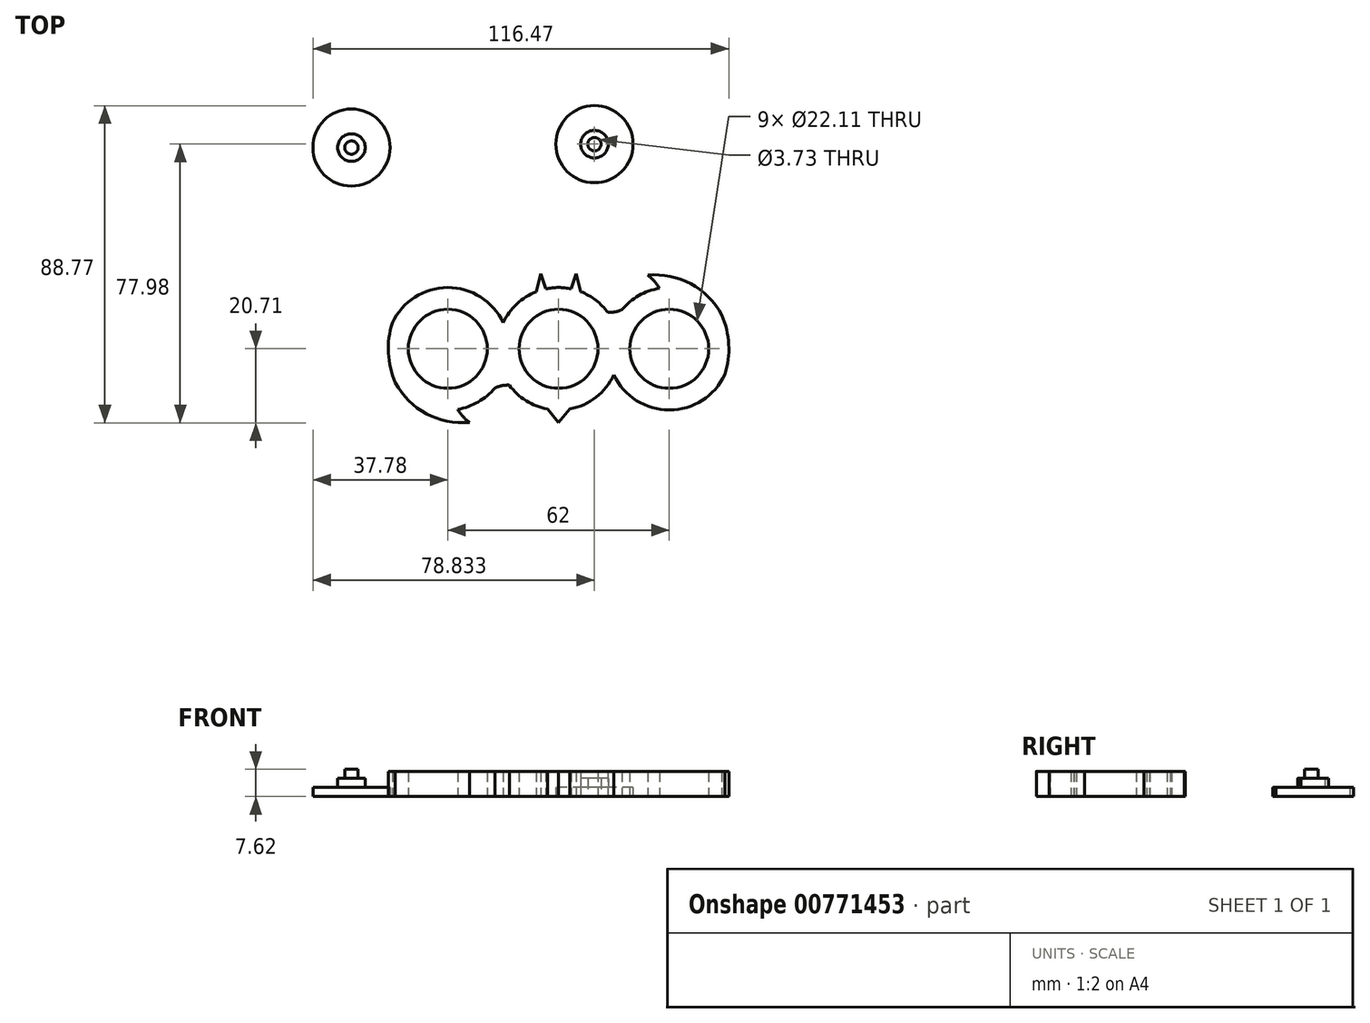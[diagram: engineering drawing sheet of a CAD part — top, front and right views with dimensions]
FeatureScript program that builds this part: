
annotation { "Feature Type Name" : "Feature", "Feature Type Description" : "" }
export const myFeature = defineFeature(function(context is Context, id is Id, definition is map)
    precondition{}
    {
        {
            var Q0;
            Q0=qCreatedBy(makeId("Top.planeOp"),FACE);
            var sketch = newSketch(context, id + "F0", { "sketchPlane" : qUnion([Q0])});
            skCircle(sketch, "E0", {"center": v(31, 0) * mm, "radius": 11.05 * mm});
            skCircle(sketch, "E1", {"center": v(-31, 0) * mm, "radius": 11.05 * mm});
            skCircle(sketch, "E2", {"center": v(0, 0) * mm, "radius": 11.05 * mm});
            skCircle(sketch, "E3", {"center": v(-31, 0) * mm, "radius": 17.15 * mm});
            skCircle(sketch, "E4", {"center": v(31, 0) * mm, "radius": 17.15 * mm});
            skCircle(sketch, "E5", {"center": v(0, 0) * mm, "radius": 17.15 * mm});
            skArc(sketch, "E6", {"start": v(-28.25, 16.92) * mm, "mid": v(-26.8, 18.94) * mm, "end": v(-24.96, 20.62) * mm});
            skArc(sketch, "E7", {"start": v(-24.96, 20.62) * mm, "mid": v(-37.01, 18.18) * mm, "end": v(-45.7, 9.47) * mm});
            skArc(sketch, "E8.MirrorCS", {"start": v(-24.96, -20.62) * mm, "mid": v(-37.01, -18.18) * mm, "end": v(-45.7, -9.47) * mm});
            skArc(sketch, "E9.MirrorCS", {"start": v(-28.25, -16.92) * mm, "mid": v(-26.8, -18.94) * mm, "end": v(-24.96, -20.62) * mm});
            skArc(sketch, "E10.MirrorCS", {"start": v(28.25, 16.92) * mm, "mid": v(26.8, 18.94) * mm, "end": v(24.96, 20.62) * mm});
            skArc(sketch, "E11.MirrorCS", {"start": v(24.96, 20.62) * mm, "mid": v(37.01, 18.18) * mm, "end": v(45.7, 9.47) * mm});
            skArc(sketch, "E12.MirrorCS", {"start": v(24.96, -20.62) * mm, "mid": v(37.01, -18.18) * mm, "end": v(45.7, -9.47) * mm});
            skArc(sketch, "E13.MirrorCS", {"start": v(28.25, -16.92) * mm, "mid": v(26.8, -18.94) * mm, "end": v(24.96, -20.62) * mm});
            skLineSegment(sketch, "E14", {"start": v(-3.1, -16.86) * mm, "end": v(0, -20.62) * mm});
            skLineSegment(sketch, "E15", {"start": v(0, -20.62) * mm, "end": v(3.15, -16.85) * mm});
            skLineSegment(sketch, "E16", {"start": v(-6.23, 15.97) * mm, "end": v(-4.98, 20.95) * mm});
            skLineSegment(sketch, "E17", {"start": v(-4.98, 20.95) * mm, "end": v(-3.55, 16.77) * mm});
            skLineSegment(sketch, "E18.MirrorCS", {"start": v(4.98, 20.95) * mm, "end": v(3.55, 16.77) * mm});
            skLineSegment(sketch, "E19.MirrorCS", {"start": v(6.23, 15.97) * mm, "end": v(4.98, 20.95) * mm});
            skArc(sketch, "E20", {"start": v(-13.8, -10.17) * mm, "mid": v(-15.85, -10.33) * mm, "end": v(-17.8, -10.94) * mm});
            skArc(sketch, "E21.MirrorCS", {"start": v(13.8, -10.17) * mm, "mid": v(15.85, -10.33) * mm, "end": v(17.8, -10.94) * mm});
            skArc(sketch, "E22.MirrorCS", {"start": v(-13.8, 10.17) * mm, "mid": v(-15.85, 10.33) * mm, "end": v(-17.8, 10.94) * mm});
            skArc(sketch, "E23.MirrorCS", {"start": v(13.8, 10.17) * mm, "mid": v(15.85, 10.33) * mm, "end": v(17.8, 10.94) * mm});
            skArc(sketch, "E24", {"start": v(-45.7, 9.47) * mm, "mid": v(-47.69, 0) * mm, "end": v(-45.7, -9.47) * mm});
            skArc(sketch, "E25.MirrorCS", {"start": v(45.7, 9.47) * mm, "mid": v(47.69, 0) * mm, "end": v(45.7, -9.47) * mm});
            skSolve(sketch);
        }
        {
            var Q0;
            {var subQ0=sQuery(id+"F0.wireOp",EDGE,"E6");Q0=makeQuery(id+"F0.imprint","IMPRINT",FACE,{"disambiguationData":[TD([[makeQuery(id+"F0.imprint","IMPRINT",EDGE,{"derivedFrom":subQ0}),1.0]])]});}
            var Q1;
            {var subQ0=sQuery(id+"F0.wireOp",EDGE,"E9.MirrorCS");Q1=makeQuery(id+"F0.imprint","IMPRINT",FACE,{"disambiguationData":[TD([[makeQuery(id+"F0.imprint","IMPRINT",EDGE,{"derivedFrom":subQ0}),-1.0]])]});}
            var Q2;
            {var subQ0=sQuery(id+"F0.wireOp",EDGE,"E22.MirrorCS");Q2=makeQuery(id+"F0.imprint","IMPRINT",FACE,{"disambiguationData":[TD([[makeQuery(id+"F0.imprint","IMPRINT",EDGE,{"derivedFrom":subQ0}),1.0]])]});}
            var Q3;
            {var subQ0=sQuery(id+"F0.wireOp",EDGE,"E5");var subQ1=sQuery(id+"F0.wireOp",EDGE,"E3");var subQ2=makeQuery(id+"F0.imprint","INTERSECT",VERTEX,{"disambiguationData":[OD(0.0)],"derivedFrom":[subQ1,subQ0]});Q3=makeQuery(id+"F0.imprint","IMPRINT",FACE,{"disambiguationData":[TD([[makeQuery(id+"F0.imprint","IMPRINT",EDGE,{"disambiguationData":[TD([[subQ2,1.0]])],"derivedFrom":subQ1}),1.0]])]});}
            var Q4;
            {var subQ0=sQuery(id+"F0.wireOp",EDGE,"E20");Q4=makeQuery(id+"F0.imprint","IMPRINT",FACE,{"disambiguationData":[TD([[makeQuery(id+"F0.imprint","IMPRINT",EDGE,{"derivedFrom":subQ0}),-1.0]])]});}
            var Q5;
            Q5=makeQuery(id+"F0.imprint","IMPRINT",FACE,{"disambiguationData":[TD([[makeQuery(id+"F0.imprint","IMPRINT",EDGE,{"derivedFrom":sQuery(id+"F0.wireOp",EDGE,"E2")}),-1.0]])]});
            var Q6;
            {var subQ0=sQuery(id+"F0.wireOp",EDGE,"E16");Q6=makeQuery(id+"F0.imprint","IMPRINT",FACE,{"disambiguationData":[TD([[makeQuery(id+"F0.imprint","IMPRINT",EDGE,{"derivedFrom":subQ0}),-1.0]])]});}
            var Q7;
            {var subQ0=sQuery(id+"F0.wireOp",EDGE,"E18.MirrorCS");Q7=makeQuery(id+"F0.imprint","IMPRINT",FACE,{"disambiguationData":[TD([[makeQuery(id+"F0.imprint","IMPRINT",EDGE,{"derivedFrom":subQ0}),1.0]])]});}
            var Q8;
            {var subQ0=sQuery(id+"F0.wireOp",EDGE,"E14");Q8=makeQuery(id+"F0.imprint","IMPRINT",FACE,{"disambiguationData":[TD([[makeQuery(id+"F0.imprint","IMPRINT",EDGE,{"derivedFrom":subQ0}),1.0]])]});}
            var Q9;
            {var subQ0=sQuery(id+"F0.wireOp",EDGE,"E5");var subQ1=sQuery(id+"F0.wireOp",EDGE,"E4");var subQ2=makeQuery(id+"F0.imprint","INTERSECT",VERTEX,{"disambiguationData":[OD(0.0)],"derivedFrom":[subQ1,subQ0]});Q9=makeQuery(id+"F0.imprint","IMPRINT",FACE,{"disambiguationData":[TD([[makeQuery(id+"F0.imprint","IMPRINT",EDGE,{"disambiguationData":[TD([[subQ2,-1.0]])],"derivedFrom":subQ1}),1.0]])]});}
            var Q10;
            {var subQ0=sQuery(id+"F0.wireOp",EDGE,"E23.MirrorCS");Q10=makeQuery(id+"F0.imprint","IMPRINT",FACE,{"disambiguationData":[TD([[makeQuery(id+"F0.imprint","IMPRINT",EDGE,{"derivedFrom":subQ0}),-1.0]])]});}
            var Q11;
            {var subQ0=sQuery(id+"F0.wireOp",EDGE,"E21.MirrorCS");Q11=makeQuery(id+"F0.imprint","IMPRINT",FACE,{"disambiguationData":[TD([[makeQuery(id+"F0.imprint","IMPRINT",EDGE,{"derivedFrom":subQ0}),1.0]])]});}
            var Q12;
            Q12=makeQuery(id+"F0.imprint","IMPRINT",FACE,{"disambiguationData":[TD([[makeQuery(id+"F0.imprint","IMPRINT",EDGE,{"derivedFrom":sQuery(id+"F0.wireOp",EDGE,"E0")}),-1.0]])]});
            var Q13;
            {var subQ0=sQuery(id+"F0.wireOp",EDGE,"E10.MirrorCS");Q13=makeQuery(id+"F0.imprint","IMPRINT",FACE,{"disambiguationData":[TD([[makeQuery(id+"F0.imprint","IMPRINT",EDGE,{"derivedFrom":subQ0}),-1.0]])]});}
            var Q14;
            {var subQ0=sQuery(id+"F0.wireOp",EDGE,"E13.MirrorCS");Q14=makeQuery(id+"F0.imprint","IMPRINT",FACE,{"disambiguationData":[TD([[makeQuery(id+"F0.imprint","IMPRINT",EDGE,{"derivedFrom":subQ0}),1.0]])]});}
            var Q15;
            Q15=makeQuery(id+"F0.imprint","IMPRINT",FACE,{"disambiguationData":[TD([[makeQuery(id+"F0.imprint","IMPRINT",EDGE,{"derivedFrom":sQuery(id+"F0.wireOp",EDGE,"E1")}),-1.0]])]});
            extrude(context, id + "F1", {"entities" : qUnion([Q0, Q1, Q2, Q3, Q4, Q5, Q6, Q7, Q8, Q9, Q10, Q11, Q12, Q13, Q14, Q15]), "depth" : 7.04 * mm, "offsetDistance" : 25.4 * mm});
        }
        {
            var Q0;
            Q0=qCreatedBy(makeId("Top.planeOp"),FACE);
            var sketch = newSketch(context, id + "F2", { "sketchPlane" : qUnion([Q0])});
            skCircle(sketch, "E26", {"center": v(-57.99, 56.32) * mm, "radius": 10.8 * mm});
            skCircle(sketch, "E27", {"center": v(-57.99, 56.32) * mm, "radius": 3.86 * mm});
            skCircle(sketch, "E28", {"center": v(-57.99, 56.32) * mm, "radius": 1.87 * mm});
            skCircle(sketch, "E29", {"center": v(10.05, 57.27) * mm, "radius": 10.8 * mm});
            skCircle(sketch, "E30", {"center": v(10.05, 57.27) * mm, "radius": 3.86 * mm});
            skCircle(sketch, "E31", {"center": v(10.05, 57.27) * mm, "radius": 1.87 * mm});
            skSolve(sketch);
        }
        {
            var Q0;
            Q0=makeQuery(id+"F2.imprint","IMPRINT",FACE,{"disambiguationData":[TD([[makeQuery(id+"F2.imprint","IMPRINT",EDGE,{"derivedFrom":sQuery(id+"F2.wireOp",EDGE,"E27")}),1.0]])]});
            var Q1;
            Q1=makeQuery(id+"F2.imprint","IMPRINT",FACE,{"disambiguationData":[TD([[makeQuery(id+"F2.imprint","IMPRINT",EDGE,{"derivedFrom":sQuery(id+"F2.wireOp",EDGE,"E30")}),1.0]])]});
            extrude(context, id + "F3", {"entities" : qUnion([Q0, Q1]), "depth" : 5.08 * mm, "offsetDistance" : 25.4 * mm});
        }
        {
            var Q0;
            Q0=qSketchRegion(id+"F2",true);
            extrude(context, id + "F4", {"entities" : qUnion([Q0]), "operationType" : NewBodyOperationType.ADD, "depth" : 2.54 * mm, "offsetDistance" : 25.4 * mm});
        }
        {
            var Q0;
            Q0=makeQuery(id+"F2.imprint","IMPRINT",FACE,{"disambiguationData":[TD([[makeQuery(id+"F2.imprint","IMPRINT",EDGE,{"derivedFrom":sQuery(id+"F2.wireOp",EDGE,"E28")}),1.0]])]});
            extrude(context, id + "F5", {"entities" : qUnion([Q0]), "operationType" : NewBodyOperationType.ADD, "depth" : 7.62 * mm, "offsetDistance" : 25.4 * mm});
        }
    });
